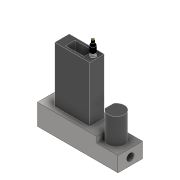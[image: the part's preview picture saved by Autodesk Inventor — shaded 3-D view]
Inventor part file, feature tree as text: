
AUTODESK INVENTOR PART (.ipt)
format: ipt  version: 2022 (Build 260153000, 153)  size: 382,464 bytes
history: native  units: mm
features: sketch x16, extrude x12, other x4, split x2, thread x2, plane x1, loft x1, boolean_combine x1, projected_geometry x1
ambient origin geometry x8: Origin, YZ Plane, XZ Plane, XY Plane, X Axis, Y Axis, Z Axis, Center Point
bodies: Solid1 (feature_tree), Solid6 (feature_tree), Solid7 (feature_tree), Solid8 (feature_tree), Solid9 (feature_tree), Solid2 (feature_tree), Solid3 (feature_tree), Solid4 (feature_tree), Solid5 (feature_tree)
feature tree (40):
  extrude  "Extrusion1"  Depth=42.0mm
  extrude  "Extrusion2"  Depth=102.0mm
  extrude  "Extrusion3"  Depth=10.0mm
  extrude  "Extrusion4"  Depth=45.0mm TaperAngle=0.0deg
  split  "Split1"
  split  "Split2"
  extrude  "Extrusion5"  Depth=60.0mm
  extrude  "Extrusion6"  Depth=95.0mm TaperAngle=0.0deg
  thread  "Thread1"  [1 undecoded]
  other  "Decal2"
  extrude  "Extrusion7"  Depth=20.0mm TaperAngle=0.0deg
  extrude  "Extrusion8"  Depth=138.0mm TaperAngle=0.0deg
  thread  "Thread2"  [1 undecoded]
  extrude  "Extrusion10"  Depth=16.65mm
  extrude  "Extrusion11"  Depth=16.2mm
  extrude  "Extrusion12"  Depth=6.0mm TaperAngle=0.0deg
  plane  "Work Plane1"
  extrude  "Extrusion13"  Depth=2.0mm TaperAngle=0.0deg
  loft  "Loft1"
  boolean_combine  "Combine1"
  sketch  "Sketch20"  dims[d69=4.0mm d70=5.0mm d71=5.0mm d72=0.0mm d73=0.0mm d74=90.0deg d75=0.0mm d76=90.0deg]
  sketch  "Sketch1"  dims[d0=138.0mm d1=42.0mm]
  sketch  "Sketch2"  dims[d2=26.0mm d3=0.0mm d4=102.0mm]
  sketch  "Sketch3"  dims[d5=10.0mm d6=0.0mm d7=12.0mm]
  sketch  "Sketch4"  dims[d8=14.0mm d9=45.0mm d10=0.0mm]
  sketch  "Sketch6"  dims[d11=21.0mm d12=60.0mm]
  sketch  "Sketch7"  dims[d13=25.0mm d14=95.0mm d15=0.0mm d16=13.0mm]
  projected_geometry  "Projected Loop2"
  sketch  "Sketch8"  dims[d17=12.0mm d18=20.0mm d19=0.0mm]
  sketch  "Sketch9"  dims[d20=20.0mm d21=0.0mm d22=138.0mm d23=0.0mm d38=30.0mm]
  sketch  "Sketch12"  dims[d39=31.8mm d40=16.65mm]
  other  "Image4"
  sketch  "Sketch13"  dims[d41=16.2mm d42=0.0mm d52=7.202mm]
  sketch  "Sketch14"  dims[d53=8.0mm d54=6.0mm d55=0.0mm]
  sketch  "Sketch16"  dims[d56=6.0mm d57=0.0mm d61=2.0mm d62=0.0mm]
  sketch  "Sketch17"  dims[d63=6.0mm d64=6.0mm d65=0.0mm]
  sketch  "Sketch18"  dims[d66=9.0mm]
  sketch  "Sketch19"  dims[d67=10.0mm d68=0.0mm]
  other  "Edges1"
  other  "Edges2"
note: 2 required parameter values undecoded (feature->parameter linkage not recoverable at this tier; creation-order binding heuristic only, values carry confidence <= 0.55)
